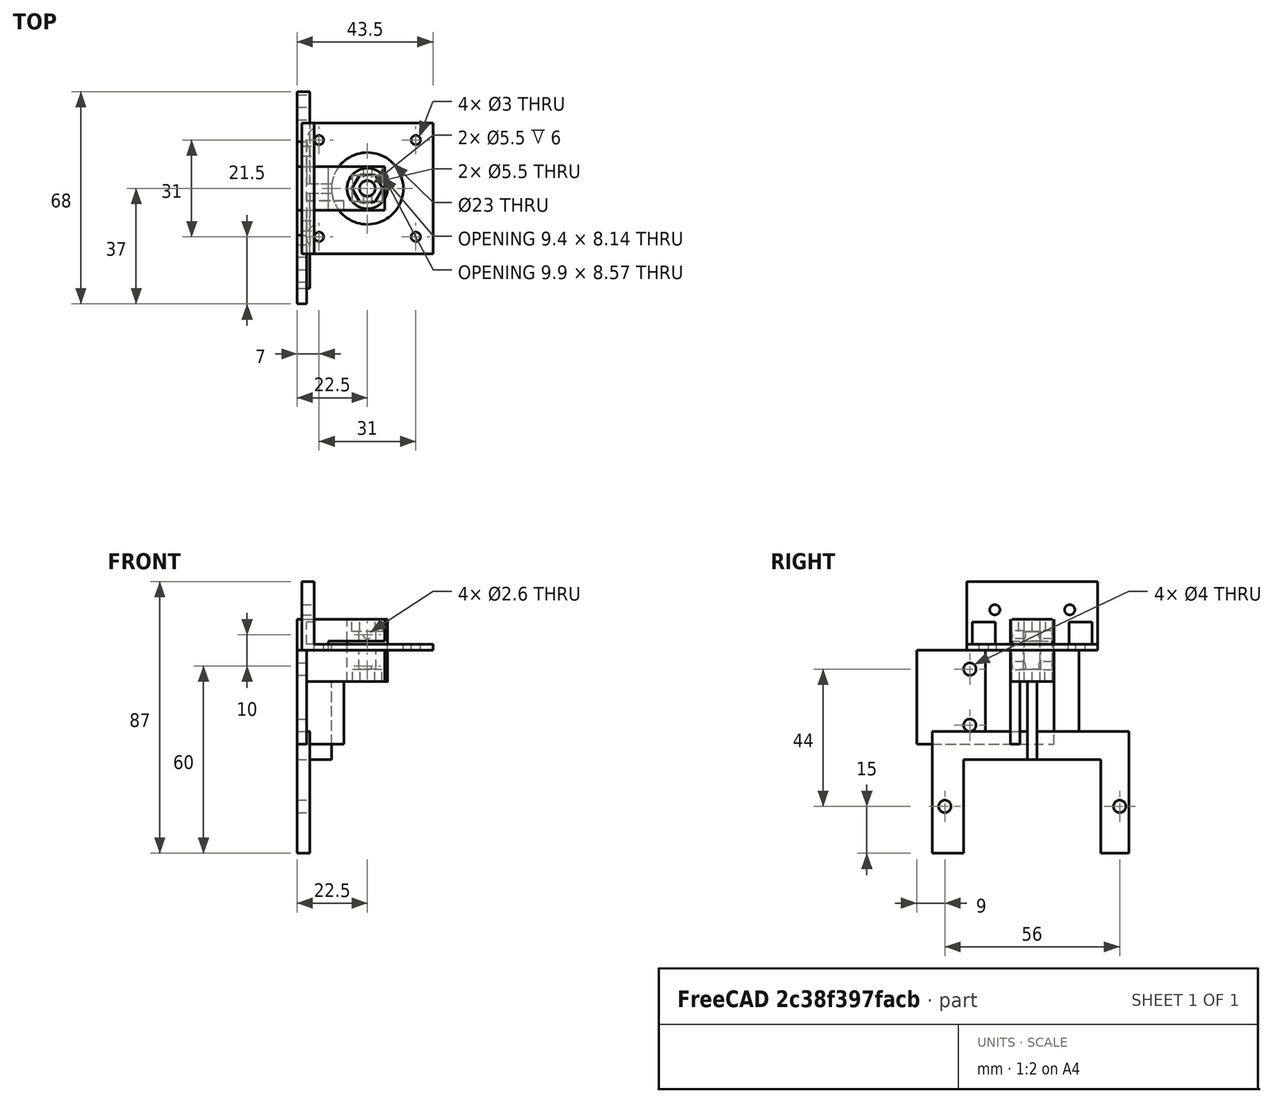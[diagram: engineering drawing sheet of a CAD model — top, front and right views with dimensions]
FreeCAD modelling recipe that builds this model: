
FCSTD DOCUMENT  (FreeCAD 0.15R4671 (Git))
Label: ネジウケ2
License: All rights reserved
LicenseURL: http://en.wikipedia.org/wiki/All_rights_reserved
objects: Part::Cylinder×19, Part::Box×14, Part::MultiFuse×12, Part::Cut×6, Part::Prism×4
note: 55 computed .brp shape members not serialized (recipe doc carries the construction recipe); baked Part::Feature solids carry a one-line shape summary decoded from their .brp

FEATURE [Part::Prism] Prism  label="ボルト"
  Circumradius = 4.7
  Height = 4
  Placement = pos=(0,0,-10) rot=(0,0,1;0rad)
  Polygon = 6
FEATURE [Part::Cylinder] Cylinder  label="円柱"
  Angle = 360
  Height = 200
  Placement = pos=(0,0,-100) rot=(0,0,1;0rad)
  Radius = 2.75
FEATURE [Part::Box] Box  label="立方体"
  Height = 7
  Length = 28
  Placement = pos=(-22.5,-7,3) rot=(0,0,1;0rad)
  Width = 14
FEATURE [Part::Prism] Prism001  label="ボルト隙間"
  Circumradius = 4.95
  Height = 4
  Placement = pos=(0,0,6) rot=(0,0,1;0rad)
  Polygon = 6
FEATURE [Part::Box] Box003  label="立方体003"
  Height = 10
  Length = 28
  Placement = pos=(-22.5,-7,-10) rot=(0,0,1;0rad)
  Width = 14
FEATURE [Part::Cylinder] Cylinder003  label="円柱003"
  Angle = 360
  Height = 20
  Placement = pos=(0,0,-10) rot=(0,0,1;0rad)
  Radius = 6.5
FEATURE [Part::Cylinder] Cylinder004  label="円柱004"
  Angle = 360
  Height = 20
  Placement = pos=(0,0,-10) rot=(0,0,1;0rad)
  Radius = 2.5
FEATURE [Part::Cylinder] Cylinder005  label="円柱005"
  Angle = 360
  Height = 20
  Placement = pos=(0,10,-5) rot=(1,0,0;1.5708rad)
  Radius = 1.3
FEATURE [Part::Cylinder] Cylinder006  label="円柱006"
  Angle = 360
  Height = 20
  Placement = pos=(0,10,5) rot=(1,0,0;1.5708rad)
  Radius = 1.3
FEATURE [Part::MultiFuse] Fusion002
  Shapes = -> [Cylinder006,Cylinder004,Cylinder005]
FEATURE [Part::Cut] Cut001
  Base = -> Cylinder003
  Tool = -> Fusion002
FEATURE [Part::Cylinder] Cylinder007  label="円柱007"
  Angle = 360
  Height = 10
  Radius = 11.5
FEATURE [Part::Cylinder] Cylinder008  label="円柱008"
  Angle = 360
  Height = 10
  Placement = pos=(-15.5,15.5,0) rot=(0,0,1;0rad)
  Radius = 1.5
FEATURE [Part::Cylinder] Cylinder009  label="円柱009"
  Angle = 360
  Height = 10
  Placement = pos=(15.5,15.5,0) rot=(0,0,1;0rad)
  Radius = 1.5
FEATURE [Part::Cylinder] Cylinder010  label="円柱010"
  Angle = 360
  Height = 10
  Placement = pos=(-15.5,-15.5,0) rot=(0,0,1;0rad)
  Radius = 1.5
FEATURE [Part::Cylinder] Cylinder011  label="円柱011"
  Angle = 360
  Height = 10
  Placement = pos=(15.5,-15.5,0) rot=(0,0,1;0rad)
  Radius = 1.5
FEATURE [Part::Box] Box004  label="立方体004"
  Height = 2
  Length = 42
  Placement = pos=(-21,-21,0) rot=(0,0,1;0rad)
  Width = 42
FEATURE [Part::Box] Box005  label="立方体005"
  Height = 22
  Length = 4
  Placement = pos=(-21,-21,0) rot=(0,0,1;0rad)
  Width = 42
FEATURE [Part::Cylinder] Cylinder012  label="円柱012"
  Angle = 360
  Height = 7
  Placement = pos=(-15.5,-15.5,2) rot=(0,0,1;0rad)
  Radius = 4
FEATURE [Part::Cylinder] Cylinder013  label="円柱013"
  Angle = 360
  Height = 7
  Placement = pos=(-15.5,15.5,2) rot=(0,0,1;0rad)
  Radius = 4
FEATURE [Part::Cylinder] Cylinder014  label="円柱014"
  Angle = 360
  Height = 10
  Placement = pos=(-23,-12,13) rot=(0,1,0;1.5708rad)
  Radius = 1.65
FEATURE [Part::Cylinder] Cylinder015  label="円柱015"
  Angle = 360
  Height = 10
  Placement = pos=(-23,12,13) rot=(0,1,0;1.5708rad)
  Radius = 1.65
FEATURE [Part::MultiFuse] Fusion003
  Shapes = -> [Box005,Box004]
FEATURE [Part::MultiFuse] Fusion004
  Shapes = -> [Cylinder015,Cylinder010,Cylinder014,Cylinder011,Cylinder007,Cylinder008,Cylinder009,Cylinder012,Cylinder013]
FEATURE [Part::Cut] Cut002
  Base = -> Fusion003
  Tool = -> Fusion004
FEATURE [Part::Box] Box006  label="立方体006"
  Height = 20
  Length = 10
  Placement = pos=(-22.5,-7,-10) rot=(0,0,1;0rad)
  Width = 14
FEATURE [Part::MultiFuse] Fusion005
  Shapes = -> [Box,Box003,Box006]
FEATURE [Part::MultiFuse] Fusion
  Shapes = -> [Prism,Cylinder,Prism001]
FEATURE [Part::Cut] Cut
  Base = -> Fusion005
  Tool = -> Fusion
FEATURE [Part::Box] Box007  label="立方体007"
  Height = 65
  Length = 3
  Placement = pos=(-22.5,-15,-65) rot=(0,0,1;0rad)
  Width = 30
FEATURE [Part::Box] Box008  label="立方体008"
  Height = 65
  Length = 11
  Placement = pos=(-22.5,-1.5,-65) rot=(0,0,1;0rad)
  Width = 3
FEATURE [Part::Cylinder] Cylinder017  label="円柱017"
  Angle = 360
  Height = 10
  Placement = pos=(-22.5,-28,-50) rot=(0,1,0;1.5708rad)
  Radius = 2
FEATURE [Part::Prism] Prism002  label="ボルト001"
  Circumradius = 4.7
  Height = 4
  Placement = pos=(0,0,-10) rot=(0,0,1;0rad)
  Polygon = 6
FEATURE [Part::Cylinder] Cylinder018  label="円柱018"
  Angle = 360
  Height = 200
  Placement = pos=(0,0,-100) rot=(0,0,1;0rad)
  Radius = 2.75
FEATURE [Part::Box] Box009  label="立方体009"
  Height = 7
  Length = 28
  Placement = pos=(-22.5,-7,3) rot=(0,0,1;0rad)
  Width = 14
FEATURE [Part::Prism] Prism003  label="ボルト隙間001"
  Circumradius = 4.95
  Height = 4
  Placement = pos=(0,0,6) rot=(0,0,1;0rad)
  Polygon = 6
FEATURE [Part::Box] Box010  label="立方体010"
  Height = 10
  Length = 28
  Placement = pos=(-22.5,-7,-10) rot=(0,0,1;0rad)
  Width = 14
FEATURE [Part::Box] Box011  label="立方体011"
  Height = 20
  Length = 10
  Placement = pos=(-22.5,-7,-10) rot=(0,0,1;0rad)
  Width = 14
FEATURE [Part::MultiFuse] Fusion008
  Shapes = -> [Box009,Box010,Box011]
FEATURE [Part::MultiFuse] Fusion009
  Shapes = -> [Prism002,Cylinder018,Prism003]
FEATURE [Part::Cut] Cut004
  Base = -> Fusion008
  Tool = -> Fusion009
FEATURE [Part::Box] Box012  label="立方体012"
  Height = 30
  Length = 3
  Placement = pos=(-22.5,-37,-30) rot=(0,0,1;0rad)
  Width = 44
FEATURE [Part::Box] Box013  label="立方体013"
  Height = 30
  Length = 15
  Placement = pos=(-22.5,-7,-30) rot=(0,0,1;0rad)
  Width = 3
FEATURE [Part::Cylinder] Cylinder019  label="円柱019"
  Angle = 360
  Height = 10
  Placement = pos=(-22.5,-20,-6) rot=(0,1,0;1.5708rad)
  Radius = 2
FEATURE [Part::Cylinder] Cylinder020  label="円柱020"
  Angle = 360
  Height = 10
  Placement = pos=(-22.5,-20,-24) rot=(0,1,0;1.5708rad)
  Radius = 2
FEATURE [Part::MultiFuse] Fusion011
  Shapes = -> [Box012,Box013]
FEATURE [Part::MultiFuse] Fusion012
  Shapes = -> [Cylinder019,Cylinder020]
FEATURE [Part::Cut] Cut005
  Base = -> Fusion011
  Tool = -> Fusion012
FEATURE [Part::MultiFuse] Fusion013
  Shapes = -> [Cut004,Cut005]
FEATURE [Part::Box] Box014  label="立方体014"
  Height = 30
  Length = 40
  Placement = pos=(-22.5,-22,-65) rot=(0,0,1;0rad)
  Width = 44
FEATURE [Part::Cylinder] Cylinder016  label="円柱016"
  Angle = 360
  Height = 10
  Placement = pos=(-22.5,28,-50) rot=(0,1,0;1.5708rad)
  Radius = 2
FEATURE [Part::Box] Box015  label="立方体015"
  Height = 39
  Length = 4
  Placement = pos=(-22.5,-32,-65) rot=(0,0,1;0rad)
  Width = 63
FEATURE [Part::MultiFuse] Fusion014
  Shapes = -> [Box014,Cylinder017,Cylinder016]
FEATURE [Part::MultiFuse] Fusion015
  Shapes = -> [Box008,Box007,Cut,Box015]
FEATURE [Part::Cut] Cut006
  Base = -> Fusion015
  Tool = -> Fusion014
